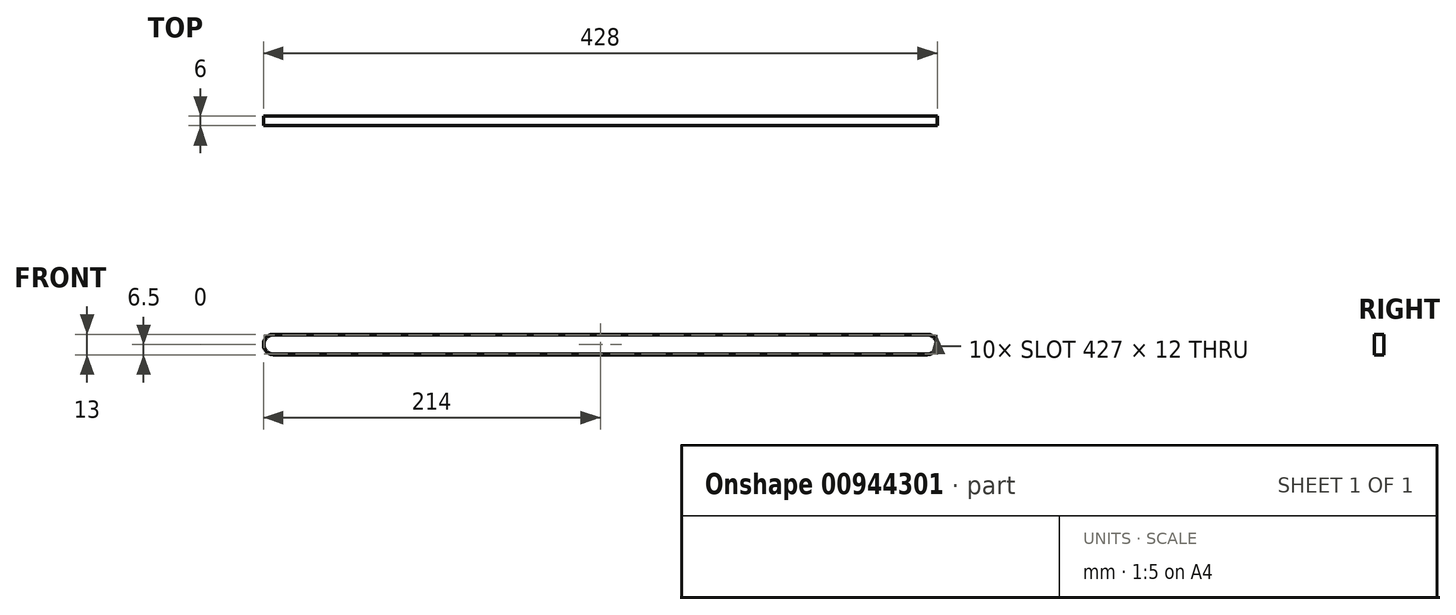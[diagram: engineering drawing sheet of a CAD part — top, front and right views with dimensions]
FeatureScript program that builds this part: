
annotation { "Feature Type Name" : "Feature", "Feature Type Description" : "" }
export const myFeature = defineFeature(function(context is Context, id is Id, definition is map)
    precondition{}
    {
        {
            var Q0;
            Q0=qCreatedBy(makeId("Front.planeOp"),FACE);
            var sketch = newSketch(context, id + "F0", { "sketchPlane" : qUnion([Q0])});
            skLineSegment(sketch, "E0", {"start": v(-69.44, 0) * mm, "end": v(69, 0) * mm, "construction": true});
            skArc(sketch, "E1", {"start": v(-207.5, 6.5) * mm, "mid": v(-214, 0) * mm, "end": v(-207.5, -6.5) * mm});
            skLineSegment(sketch, "E2", {"start": v(-207.5, 6.5) * mm, "end": v(0, 6.5) * mm});
            skLineSegment(sketch, "E3", {"start": v(-207.5, -6.5) * mm, "end": v(0, -6.5) * mm});
            skArc(sketch, "E4", {"start": v(-207.5, 6) * mm, "mid": v(-213.5, 0) * mm, "end": v(-207.5, -6) * mm});
            skLineSegment(sketch, "E5", {"start": v(-207.5, 6) * mm, "end": v(0, 6) * mm});
            skLineSegment(sketch, "E6", {"start": v(-207.5, -6) * mm, "end": v(0, -6) * mm});
            skLineSegment(sketch, "E7.MirrorCS", {"start": v(207.5, -6.5) * mm, "end": v(0, -6.5) * mm});
            skLineSegment(sketch, "E8.MirrorCS", {"start": v(69.44, 0) * mm, "end": v(-69, 0) * mm, "construction": true});
            skArc(sketch, "E9.MirrorCS", {"start": v(207.5, 6) * mm, "mid": v(213.5, 0) * mm, "end": v(207.5, -6) * mm});
            skLineSegment(sketch, "E10.MirrorCS", {"start": v(207.5, 6) * mm, "end": v(0, 6) * mm});
            skLineSegment(sketch, "E11.MirrorCS", {"start": v(207.5, 6.5) * mm, "end": v(0, 6.5) * mm});
            skArc(sketch, "E12.MirrorCS", {"start": v(207.5, 6.5) * mm, "mid": v(214, 0) * mm, "end": v(207.5, -6.5) * mm});
            skLineSegment(sketch, "E13.MirrorCS", {"start": v(207.5, -6) * mm, "end": v(0, -6) * mm});
            skSolve(sketch);
        }
        {
            var Q0;
            Q0=makeQuery(id+"F0.imprint","IMPRINT",FACE,{"disambiguationData":[TD([[makeQuery(id+"F0.imprint","IMPRINT",EDGE,{"derivedFrom":sQuery(id+"F0.wireOp",EDGE,"E1")}),1.0]])]});
            extrude(context, id + "F1", {"entities" : qUnion([Q0]), "depth" : 6 * mm, "offsetDistance" : 25 * mm});
        }
    });
